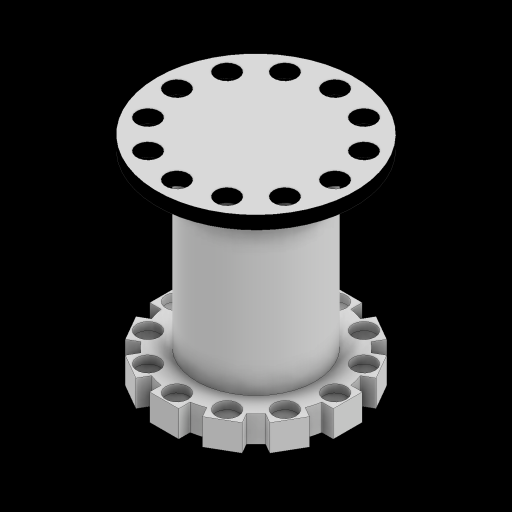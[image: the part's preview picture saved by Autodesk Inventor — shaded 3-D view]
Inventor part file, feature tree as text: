
AUTODESK INVENTOR PART (.ipt)
format: ipt  version: 2023 (Build 270158000, 158)  size: 357,888 bytes
history: native  units: mm
features: sketch x5, extrude x4, fillet x1
ambient origin geometry x8: Origin, YZ Plane, XZ Plane, XY Plane, X Axis, Y Axis, Z Axis, Center Point
bodies: Solid1 (feature_tree)
feature tree (10):
  extrude  "Extrusion1"  Depth=150.0mm
  extrude  "Extrusion2"  Depth=120.0mm TaperAngle=360.0deg
  extrude  "Extrusion9"  Depth=10.0mm
  extrude  "Extrusion10"  Depth=20.0mm TaperAngle=360.0deg
  fillet  "Fillet1"  Radius=120.0mm
  sketch  "Sketch8"  dims[d72=17.0mm d73=120.0mm d75=360.0deg d77=10.0mm d78=0.0mm d91=4.0mm d92=124.403mm d93=23.006mm d94=14.13mm d95=0.5mm d97=14.13mm d98=0.5mm d99=120.0mm d101=360.0deg d103=120.0mm d105=360.0deg]
  sketch  "Sketch1"  dims[d0=150.0mm d1=120.0mm]
  sketch  "Sketch2"  dims[d2=17.0mm d3=120.0mm d5=360.0deg]
  sketch  "Sketch3"  dims[d7=10.0mm d8=0.0mm d9=90.0mm]
  sketch  "Sketch7"  dims[d10=130.0mm d11=0.0mm d67=120.0mm d68=360.0deg d69=20.0mm d70=0.0mm d71=120.0mm]
